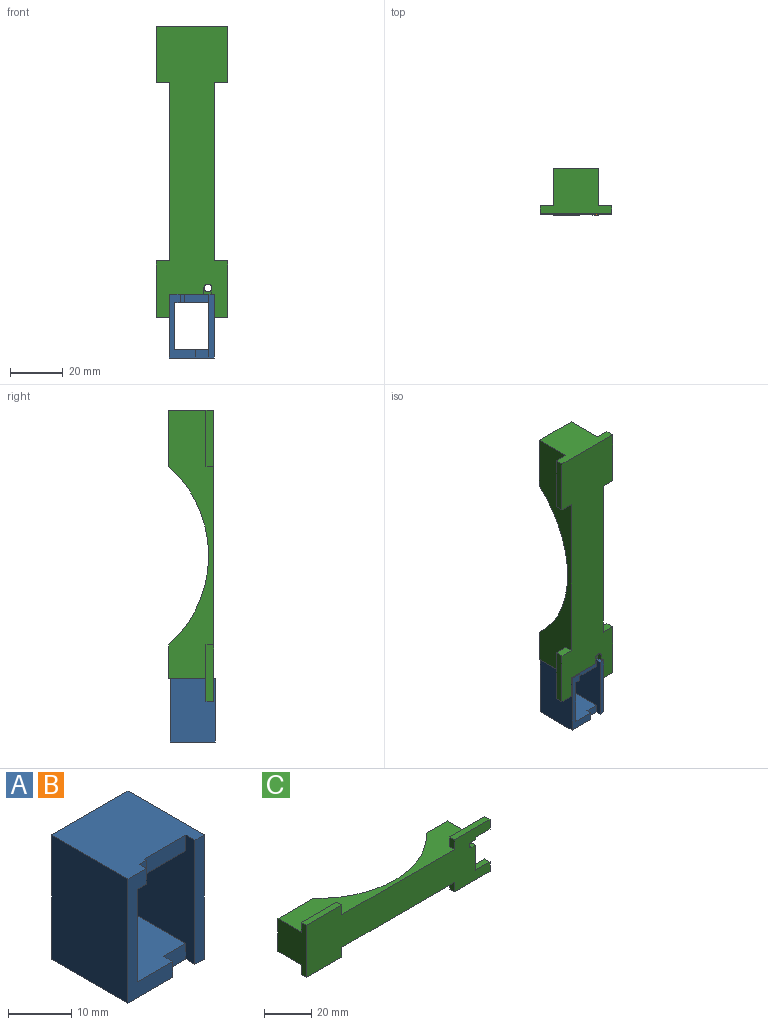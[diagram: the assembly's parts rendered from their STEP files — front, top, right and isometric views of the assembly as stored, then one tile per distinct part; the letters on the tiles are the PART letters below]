
ASSEMBLY  parts=3 mates=1
PART A: 17 faces, bbox 17x17x24 mm
  f0: plane 24x2.05mm, normal (0,-1,0), area 49.2mm2, adj f1,f4,f7,f8
  f1: plane 17x17mm, normal (0,0,1), area 267.9mm2, adj f0,f2,f4,f5,f6,f8,f13,f14
  f2: plane 24x9.95mm, normal (0,-1,0), area 79.4mm2, adj f1,f3,f6,f7,f9,f10,f11,f14
  f3: plane 17x12.9mm, normal (0,0,-1), area 198.2mm2, adj f2,f5,f8,f9,f13,f14,f15,f16
  f4: plane 24x17mm, normal (1,0,0), area 408mm2, adj f0,f1,f5,f7
  f5: plane 24x17mm, normal (0,1,0), area 177.1mm2, adj f1,f3,f4,f6,f7,f8,f9,f10
  f6: plane 24x17mm, normal (-1,0,0), area 408mm2, adj f1,f2,f5,f7
  f7: plane 17x17mm, normal (0,0,-1), area 279mm2, adj f0,f2,f4,f5,f6,f8,f11,f12
  f8: plane 24x17mm, normal (-1,0,0), area 316.5mm2, adj f0,f1,f3,f5,f7,f10,f12,f15
  f9: plane 17.9x17mm, normal (1,0,0), area 304.3mm2, adj f2,f3,f5,f10
  f10: plane 17x12.9mm, normal (0,0,1), area 209.3mm2, adj f2,f5,f8,f9,f11,f12
  f11: plane 3.05x2mm, normal (1,0,0), area 6.1mm2, adj f2,f7,f10,f12
  f12: plane 5x3.05mm, normal (0,-1,0), area 15.2mm2, adj f7,f8,f10,f11
  f13: plane 3.05x1.6mm, normal (0,-1,0), area 4.9mm2, adj f1,f3,f14,f16
  f14: plane 3.05x1.6mm, normal (1,0,0), area 4.9mm2, adj f1,f2,f3,f13
  f15: plane 9.29x3.05mm, normal (0,-1,0), area 28.3mm2, adj f1,f3,f8,f16
  f16: plane 3.05x0.4mm, normal (1,0,0), area 1.2mm2, adj f1,f3,f13,f15
PART B: same geometry as A
PART C: 28 faces, bbox 110x17x27 mm
  f0: plane 110x27mm, normal (0,-1,0), area 2137.9mm2, adj f1,f2,f3,f4,f5,f6,f9,f12
  f1: plane 17x17mm, normal (1,0,0), area 283mm2, adj f0,f4,f5,f7,f23,f24,f25,f26
  f2: cylinder r=1.5mm len=17mm, axis (0,1,0), area 151.5mm2, adj f0,f7,f25,f26,f27
  f3: plane 5x3mm, normal (1,0,0), area 15mm2, adj f0,f17,f19,f23
  f4: plane 101.41x17mm, normal (0,0,1), area 921.1mm2, adj f0,f1,f7,f8,f9,f10,f11,f12
  f5: plane 101.41x17mm, normal (0,0,-1), area 921.1mm2, adj f0,f1,f7,f8,f9,f10,f17,f18
  f6: plane 5x3mm, normal (1,0,0), area 15mm2, adj f0,f11,f13,f24
  f7: plane 17x12.65mm, normal (0,1,0), area 207.9mm2, adj f1,f2,f4,f5,f10
  f8: plane 21.24x17mm, normal (0,1,0), area 361mm2, adj f4,f5,f9,f10
  f9: plane 27x17mm, normal (-1,0,0), area 319mm2, adj f0,f4,f5,f8,f14,f16,f20,f22
  f10: cylinder r=45.5mm len=67.53mm, axis (0,0,1), area 1293.5mm2, adj f4,f5,f7,f8
  f11: plane 21.24x5mm, normal (0,1,0), area 106.2mm2, adj f4,f6,f12,f13,f24
  f12: plane 5x3mm, normal (-1,0,0), area 15mm2, adj f0,f4,f11,f13
  f13: plane 21.24x3mm, normal (0,0,1), area 63.7mm2, adj f0,f6,f11,f12
  f14: plane 21.24x5mm, normal (0,1,0), area 106.2mm2, adj f4,f9,f15,f16
  f15: plane 5x3mm, normal (1,0,0), area 15mm2, adj f0,f4,f14,f16
  f16: plane 21.24x3mm, normal (0,0,1), area 63.7mm2, adj f0,f9,f14,f15
  f17: plane 21.24x5mm, normal (0,1,0), area 106.2mm2, adj f3,f5,f18,f19,f23
  f18: plane 5x3mm, normal (-1,0,0), area 15mm2, adj f0,f5,f17,f19
  f19: plane 21.24x3mm, normal (0,0,-1), area 63.7mm2, adj f0,f3,f17,f18
  f20: plane 21.24x5mm, normal (0,1,0), area 106.2mm2, adj f5,f9,f21,f22
  f21: plane 5x3mm, normal (1,0,0), area 15mm2, adj f0,f5,f20,f22
  f22: plane 21.24x3mm, normal (0,0,-1), area 63.7mm2, adj f0,f9,f20,f21
  f23: plane 8.59x3mm, normal (0,0,1), area 25.8mm2, adj f0,f1,f3,f17
  f24: plane 8.59x3mm, normal (0,0,-1), area 25.8mm2, adj f0,f1,f6,f11
  f25: plane 2.26x2mm, normal (0,0,-1), area 4.5mm2, adj f0,f1,f2,f27
  f26: plane 2.28x2mm, normal (0,0,1), area 4.6mm2, adj f0,f1,f2,f27
  f27: plane 2.98x2.28mm, normal (0,-1,0), area 3.8mm2, adj f1,f2,f25,f26
PLACE A t=(18.44,13.49,-32.01)mm
PLACE B t=(18.44,13.49,-32.01)mm
PLACE C rot(axis=(0,1,0),90deg) t=(9.98,13.93,38.4)mm
MATE planar C.f1 <-> A.f1  axis (0,0,-1) through (18.35,14.09,-8.01)mm
